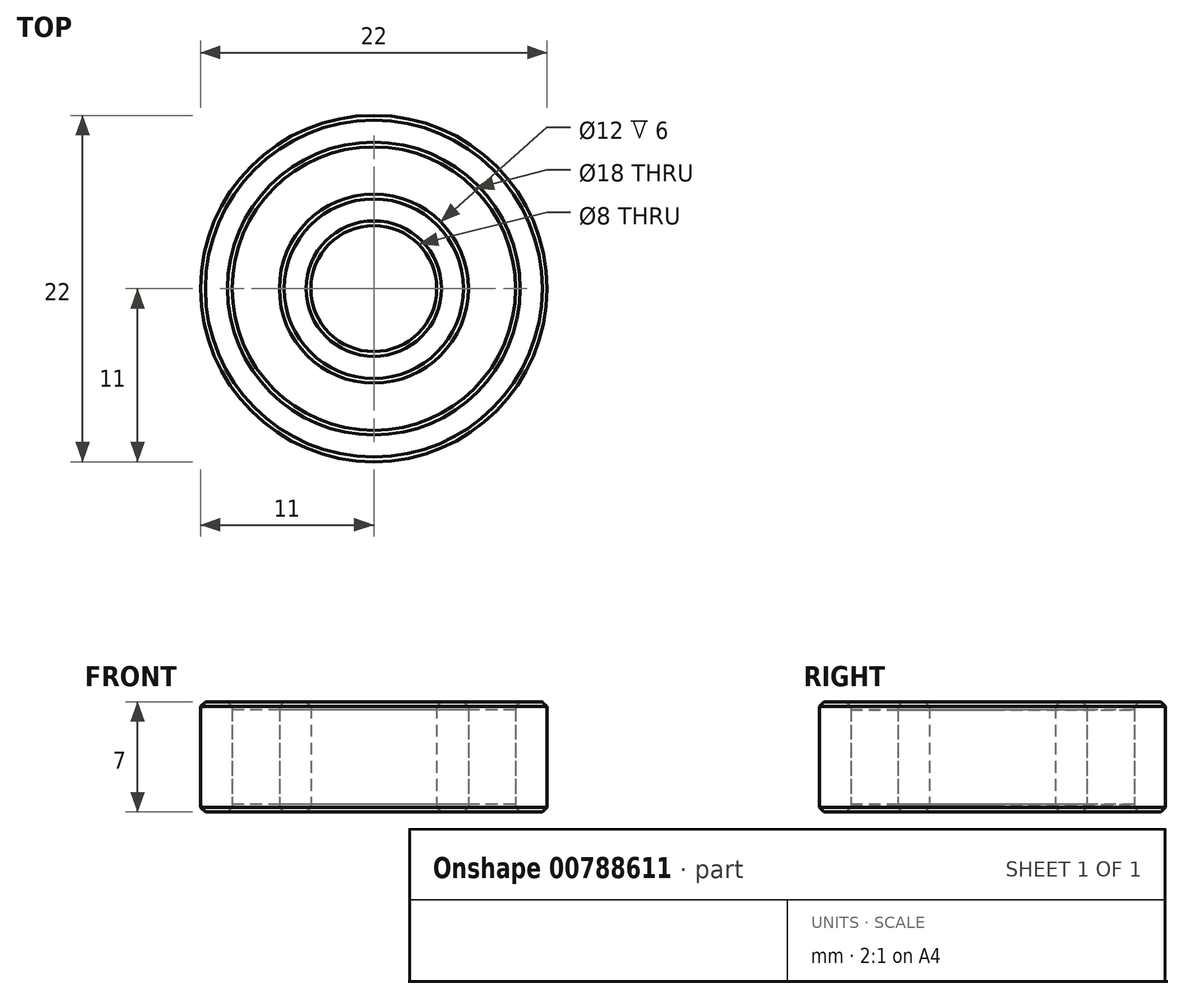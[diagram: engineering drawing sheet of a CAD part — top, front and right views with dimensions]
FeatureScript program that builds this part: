
annotation { "Feature Type Name" : "Feature", "Feature Type Description" : "" }
export const myFeature = defineFeature(function(context is Context, id is Id, definition is map)
    precondition{}
    {
        {
            var Q0;
            Q0=qCreatedBy(makeId("Top.planeOp"),FACE);
            var sketch = newSketch(context, id + "F0", { "sketchPlane" : qUnion([Q0])});
            skCircle(sketch, "E0", {"center": v(0, 0) * mm, "radius": 11 * mm});
            skCircle(sketch, "E1", {"center": v(0, 0) * mm, "radius": 4 * mm});
            skCircle(sketch, "E2", {"center": v(0, 0) * mm, "radius": 6 * mm});
            skCircle(sketch, "E3", {"center": v(0, 0) * mm, "radius": 9 * mm});
            skSolve(sketch);
        }
        {
            var Q0;
            Q0=makeQuery(id+"F0.imprint","IMPRINT",FACE,{"disambiguationData":[TD([[makeQuery(id+"F0.imprint","IMPRINT",EDGE,{"derivedFrom":sQuery(id+"F0.wireOp",EDGE,"E0")}),1.0]])]});
            var Q1;
            Q1=makeQuery(id+"F0.imprint","IMPRINT",FACE,{"disambiguationData":[TD([[makeQuery(id+"F0.imprint","IMPRINT",EDGE,{"derivedFrom":sQuery(id+"F0.wireOp",EDGE,"E1")}),-1.0]])]});
            extrude(context, id + "F1", {"entities" : qUnion([Q0, Q1]), "endBound" : BoundingType.SYMMETRIC, "depth" : 7 * mm, "offsetDistance" : 25 * mm});
        }
        {
            var Q0;
            Q0=makeQuery(id+"F0.imprint","IMPRINT",FACE,{"disambiguationData":[TD([[makeQuery(id+"F0.imprint","IMPRINT",EDGE,{"derivedFrom":sQuery(id+"F0.wireOp",EDGE,"E2")}),-1.0]])]});
            extrude(context, id + "F2", {"entities" : qUnion([Q0]), "endBound" : BoundingType.SYMMETRIC, "depth" : 6 * mm, "offsetDistance" : 25 * mm});
        }
        {
            var Q0;
            Q0=makeQuery(id+"F1.opExtrude","CAP_EDGE",EDGE,{"disambiguationData":[OSD([sQuery(id+"F0.wireOp",EDGE,"E0")])],"isStart":false});
            var Q1;
            Q1=makeQuery(id+"F1.opExtrude","CAP_EDGE",EDGE,{"disambiguationData":[OSD([sQuery(id+"F0.wireOp",EDGE,"E1")])],"isStart":false});
            var Q2;
            Q2=makeQuery(id+"F1.opExtrude","CAP_EDGE",EDGE,{"disambiguationData":[OSD([sQuery(id+"F0.wireOp",EDGE,"E3")])],"isStart":false});
            var Q3;
            Q3=makeQuery(id+"F1.opExtrude","CAP_EDGE",EDGE,{"disambiguationData":[OSD([sQuery(id+"F0.wireOp",EDGE,"E2")])],"isStart":false});
            var Q4;
            Q4=makeQuery(id+"F1.opExtrude","CAP_EDGE",EDGE,{"disambiguationData":[OSD([sQuery(id+"F0.wireOp",EDGE,"E0")])],"isStart":true});
            var Q5;
            Q5=makeQuery(id+"F1.opExtrude","CAP_EDGE",EDGE,{"disambiguationData":[OSD([sQuery(id+"F0.wireOp",EDGE,"E3")])],"isStart":true});
            var Q6;
            Q6=makeQuery(id+"F1.opExtrude","CAP_EDGE",EDGE,{"disambiguationData":[OSD([sQuery(id+"F0.wireOp",EDGE,"E2")])],"isStart":true});
            var Q7;
            Q7=makeQuery(id+"F1.opExtrude","CAP_EDGE",EDGE,{"disambiguationData":[OSD([sQuery(id+"F0.wireOp",EDGE,"E1")])],"isStart":true});
            chamfer(context, id + "F3", {"entities" : qUnion([Q0, Q1, Q2, Q3, Q4, Q5, Q6, Q7]), "width" : 0.3 * mm, "tangentPropagation" : true});
        }
    });
